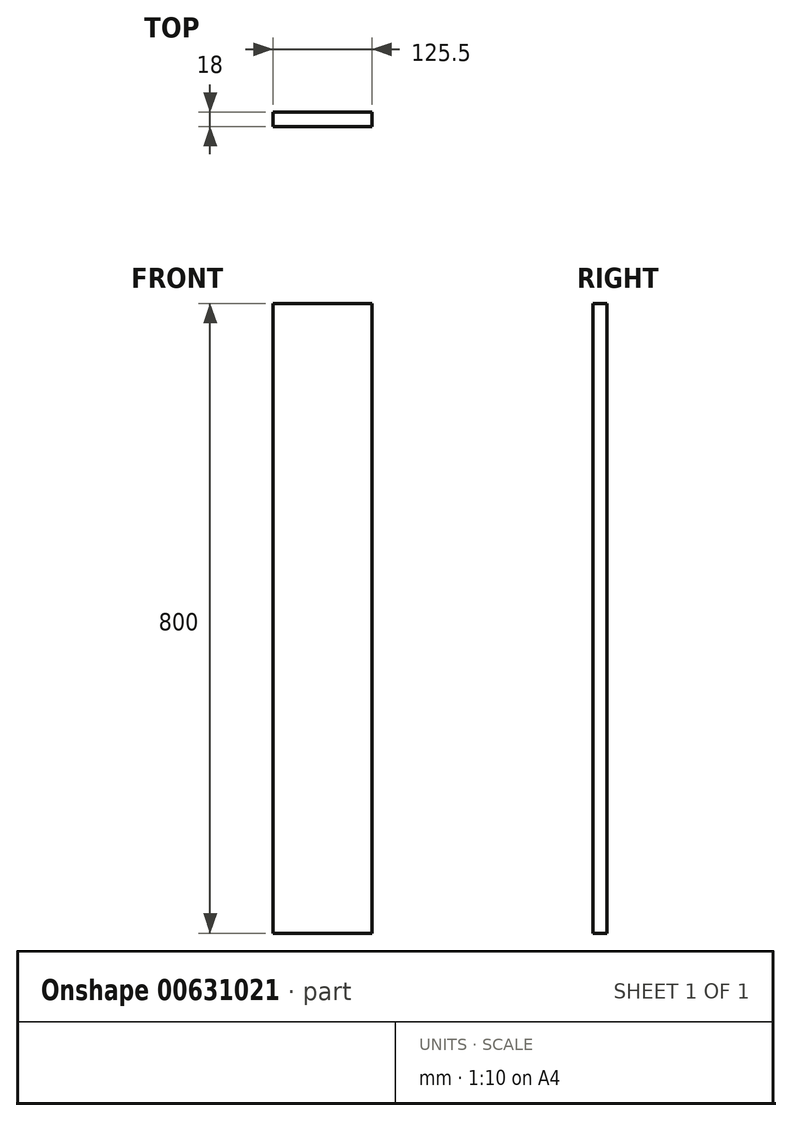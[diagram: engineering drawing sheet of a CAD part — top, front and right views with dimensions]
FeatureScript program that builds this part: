
annotation { "Feature Type Name" : "Feature", "Feature Type Description" : "" }
export const myFeature = defineFeature(function(context is Context, id is Id, definition is map)
    precondition{}
    {
        {
            var Q0;
            Q0=qCreatedBy(makeId("Front.planeOp"),FACE);
            var sketch = newSketch(context, id + "F0", { "sketchPlane" : qUnion([Q0])});
            skLineSegment(sketch, "E0.bottom", {"start": v(0, 0) * mm, "end": v(125.5, 0) * mm});
            skLineSegment(sketch, "E0.top", {"start": v(0, -800) * mm, "end": v(125.5, -800) * mm});
            skLineSegment(sketch, "E0.left", {"start": v(0, 0) * mm, "end": v(0, -800) * mm});
            skLineSegment(sketch, "E0.right", {"start": v(125.5, 0) * mm, "end": v(125.5, -800) * mm});
            skSolve(sketch);
        }
        {
            var Q0;
            Q0 = qSketchRegion(id + "F0", true);
            extrude(context, id + "F1", {"entities" : qUnion([Q0]), "oppositeDirection" : true, "depth" : 18 * mm, "offsetDistance" : 25 * mm});
        }
    });
